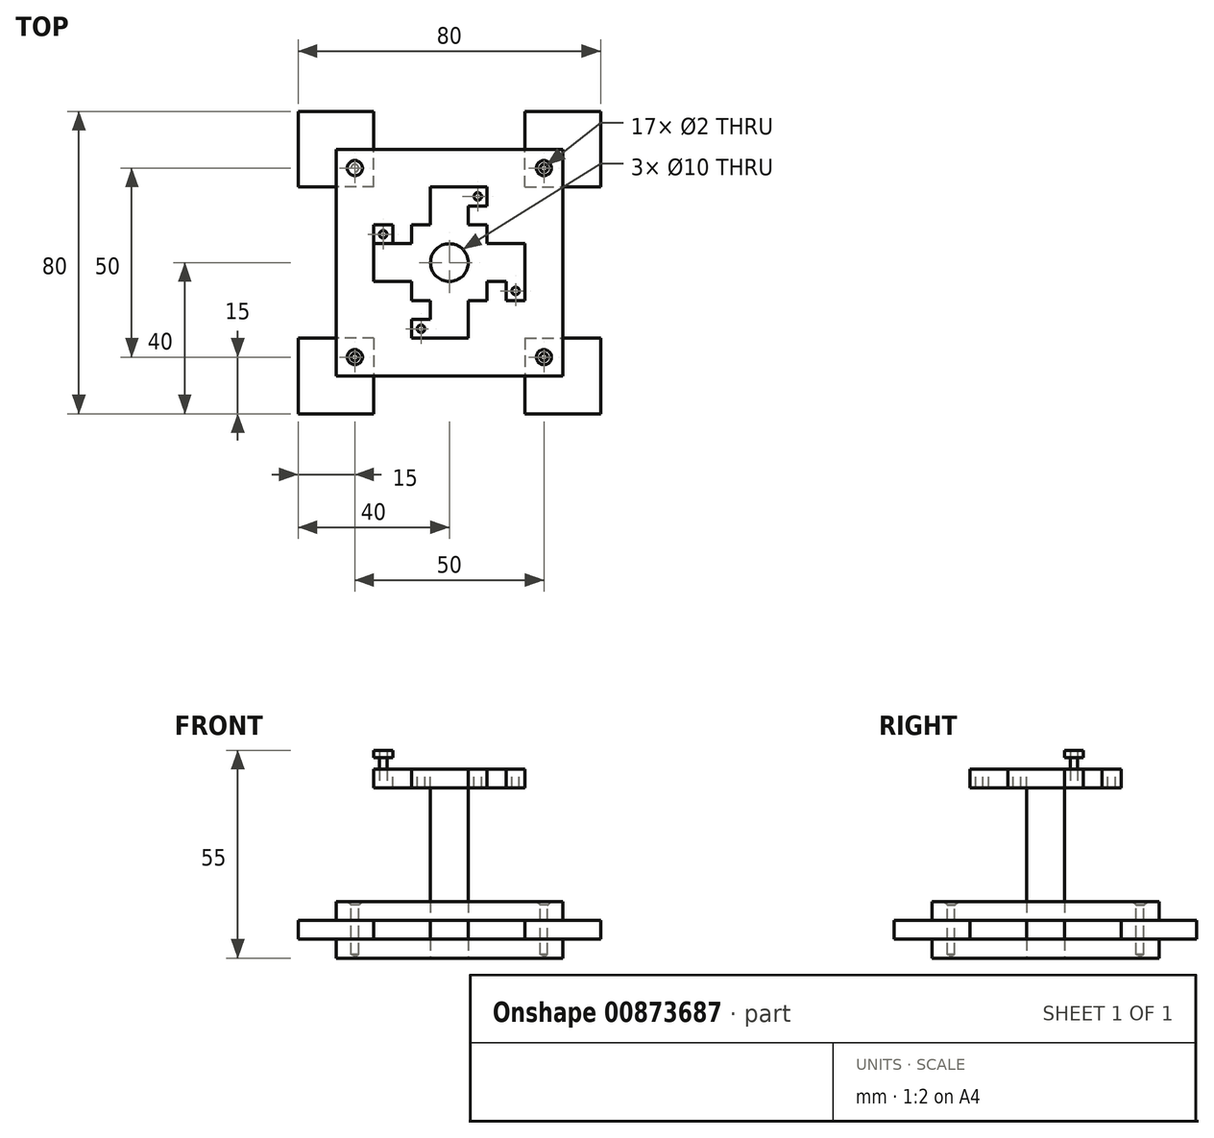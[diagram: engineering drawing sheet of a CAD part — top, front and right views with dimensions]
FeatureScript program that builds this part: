
annotation { "Feature Type Name" : "Feature", "Feature Type Description" : "" }
export const myFeature = defineFeature(function(context is Context, id is Id, definition is map)
    precondition{}
    {
        {
            var Q0;
            Q0=qCreatedBy(makeId("Top.planeOp"),FACE);
            var sketch = newSketch(context, id + "F0", { "sketchPlane" : qUnion([Q0])});
            skLineSegment(sketch, "E0.bottom", {"start": v(-30, 30) * mm, "end": v(30, 30) * mm});
            skLineSegment(sketch, "E0.top", {"start": v(-30, -30) * mm, "end": v(30, -30) * mm});
            skLineSegment(sketch, "E0.left", {"start": v(-30, 30) * mm, "end": v(-30, -30) * mm});
            skLineSegment(sketch, "E0.right", {"start": v(30, 30) * mm, "end": v(30, -30) * mm});
            skPoint(sketch, "E0.middle", {"position": v(0, 0) * mm});
            skSolve(sketch);
        }
        {
            var Q0;
            Q0 = qSketchRegion(id + "F0", true);
            extrude(context, id + "F1", {"entities" : qUnion([Q0]), "depth" : 5 * mm, "offsetDistance" : 25 * mm});
        }
        {
            var Q0;
            Q0=makeQuery(id+"F1.opExtrude","CAP_FACE",FACE,{"disambiguationData":[OSD([sQuery(id+"F0.wireOp",EDGE,"E0.bottom"),sQuery(id+"F0.wireOp",EDGE,"E0.top"),sQuery(id+"F0.wireOp",EDGE,"E0.left"),sQuery(id+"F0.wireOp",EDGE,"E0.right")])],"isStart":false});
            var sketch = newSketch(context, id + "F2", { "sketchPlane" : qUnion([Q0])});
            skLineSegment(sketch, "E1.bottom", {"start": v(-20, 20) * mm, "end": v(-40, 20) * mm});
            skLineSegment(sketch, "E1.top", {"start": v(-20, 40) * mm, "end": v(-40, 40) * mm});
            skLineSegment(sketch, "E1.left", {"start": v(-20, 20) * mm, "end": v(-20, 40) * mm});
            skLineSegment(sketch, "E1.right", {"start": v(-40, 20) * mm, "end": v(-40, 40) * mm});
            skPoint(sketch, "E1.middle", {"position": v(-30, 30) * mm});
            skSolve(sketch);
        }
        {
            var Q0;
            Q0 = qSketchRegion(id + "F2", true);
            extrude(context, id + "F3", {"entities" : qUnion([Q0]), "depth" : 5 * mm, "offsetDistance" : 25 * mm});
        }
        {
            var Q0;
            Q0=makeQuery(id+"F3.opExtrude","CAP_FACE",FACE,{"disambiguationData":[OSD([sQuery(id+"F2.wireOp",EDGE,"E1.bottom"),sQuery(id+"F2.wireOp",EDGE,"E1.top"),sQuery(id+"F2.wireOp",EDGE,"E1.left"),sQuery(id+"F2.wireOp",EDGE,"E1.right")])],"isStart":false});
            var sketch = newSketch(context, id + "F4", { "sketchPlane" : qUnion([Q0])});
            skPoint(sketch, "E2.middle", {"position": v(0, 0) * mm});
            skLineSegment(sketch, "E3.0.0", {"start": v(-30, 30) * mm, "end": v(-30, -30) * mm});
            skLineSegment(sketch, "E3.0.1", {"start": v(-30, -30) * mm, "end": v(30, -30) * mm});
            skLineSegment(sketch, "E3.0.2", {"start": v(30, -30) * mm, "end": v(30, 30) * mm});
            skLineSegment(sketch, "E3.0.3", {"start": v(30, 30) * mm, "end": v(-30, 30) * mm});
            skSolve(sketch);
        }
        {
            var Q0;
            Q0 = qSketchRegion(id + "F4", true);
            extrude(context, id + "F5", {"entities" : qUnion([Q0]), "depth" : 5 * mm, "offsetDistance" : 25 * mm});
        }
        {
            var Q0;
            Q0=makeQuery(id+"F3.opExtrude","SWEPT_BODY",BODY,{"disambiguationData":[OSD([sQuery(id+"F2.wireOp",EDGE,"E1.bottom"),sQuery(id+"F2.wireOp",EDGE,"E1.top"),sQuery(id+"F2.wireOp",EDGE,"E1.left"),sQuery(id+"F2.wireOp",EDGE,"E1.right")])]});
            var Q1;
            Q1=qCreatedBy(makeId("Right.planeOp"),FACE);
            mirror(context, id + "F6", {"entities" : qUnion([Q0]), "mirrorPlane" : qUnion([Q1])});
        }
        {
            var Q0;
            Q0=makeQuery(id+"F3.opExtrude","SWEPT_BODY",BODY,{"disambiguationData":[OSD([sQuery(id+"F2.wireOp",EDGE,"E1.bottom"),sQuery(id+"F2.wireOp",EDGE,"E1.top"),sQuery(id+"F2.wireOp",EDGE,"E1.left"),sQuery(id+"F2.wireOp",EDGE,"E1.right")])]});
            var Q1;
            Q1=makeQuery(id+"F6.opPattern","COPY",BODY,{"derivedFrom":makeQuery(id+"F3.opExtrude","SWEPT_BODY",BODY,{"disambiguationData":[OSD([sQuery(id+"F2.wireOp",EDGE,"E1.bottom"),sQuery(id+"F2.wireOp",EDGE,"E1.top"),sQuery(id+"F2.wireOp",EDGE,"E1.left"),sQuery(id+"F2.wireOp",EDGE,"E1.right")])]}),"instanceName":"1"});
            var Q2;
            Q2=qCreatedBy(makeId("Front.planeOp"),FACE);
            mirror(context, id + "F7", {"entities" : qUnion([Q0, Q1]), "mirrorPlane" : qUnion([Q2])});
        }
        {
            var Q0;
            Q0=makeQuery(id+"F5.opExtrude","CAP_FACE",FACE,{"disambiguationData":[OSD([sQuery(id+"F4.wireOp",EDGE,"E3.0.0"),sQuery(id+"F4.wireOp",EDGE,"E3.0.1"),sQuery(id+"F4.wireOp",EDGE,"E3.0.2"),sQuery(id+"F4.wireOp",EDGE,"E3.0.3")])],"isStart":false});
            var sketch = newSketch(context, id + "F8", { "sketchPlane" : qUnion([Q0])});
            skPoint(sketch, "E4", {"position": v(-25, 25) * mm});
            skPoint(sketch, "E5.MirrorP", {"position": v(-25, -25) * mm});
            skPoint(sketch, "E6.MirrorP", {"position": v(25, 25) * mm});
            skPoint(sketch, "E7.MirrorP", {"position": v(25, -25) * mm});
            skSolve(sketch);
        }
        {
            var Q0;
            Q0=sQuery(id+"F8.wireOp",VERTEX,"E4");
            var Q1;
            Q1=sQuery(id+"F8.wireOp",VERTEX,"E6.MirrorP");
            var Q2;
            Q2=sQuery(id+"F8.wireOp",VERTEX,"E5.MirrorP");
            var Q3;
            Q3=sQuery(id+"F8.wireOp",VERTEX,"E7.MirrorP");
            var Q4;
            Q4=makeQuery(id+"F3.opExtrude","SWEPT_BODY",BODY,{"disambiguationData":[OSD([sQuery(id+"F2.wireOp",EDGE,"E1.bottom"),sQuery(id+"F2.wireOp",EDGE,"E1.top"),sQuery(id+"F2.wireOp",EDGE,"E1.left"),sQuery(id+"F2.wireOp",EDGE,"E1.right")])]});
            var Q5;
            Q5=makeQuery(id+"F6.opPattern","COPY",BODY,{"derivedFrom":makeQuery(id+"F3.opExtrude","SWEPT_BODY",BODY,{"disambiguationData":[OSD([sQuery(id+"F2.wireOp",EDGE,"E1.bottom"),sQuery(id+"F2.wireOp",EDGE,"E1.top"),sQuery(id+"F2.wireOp",EDGE,"E1.left"),sQuery(id+"F2.wireOp",EDGE,"E1.right")])]}),"instanceName":"1"});
            var Q6;
            Q6=makeQuery(id+"F1.opExtrude","SWEPT_BODY",BODY,{"disambiguationData":[OSD([sQuery(id+"F0.wireOp",EDGE,"E0.bottom"),sQuery(id+"F0.wireOp",EDGE,"E0.top"),sQuery(id+"F0.wireOp",EDGE,"E0.left"),sQuery(id+"F0.wireOp",EDGE,"E0.right")])]});
            var Q7;
            Q7=makeQuery(id+"F5.opExtrude","SWEPT_BODY",BODY,{"disambiguationData":[OSD([sQuery(id+"F4.wireOp",EDGE,"E3.0.0"),sQuery(id+"F4.wireOp",EDGE,"E3.0.1"),sQuery(id+"F4.wireOp",EDGE,"E3.0.2"),sQuery(id+"F4.wireOp",EDGE,"E3.0.3")])]});
            var Q8;
            Q8=makeQuery(id+"F7.opPattern","COPY",BODY,{"derivedFrom":makeQuery(id+"F3.opExtrude","SWEPT_BODY",BODY,{"disambiguationData":[OSD([sQuery(id+"F2.wireOp",EDGE,"E1.bottom"),sQuery(id+"F2.wireOp",EDGE,"E1.top"),sQuery(id+"F2.wireOp",EDGE,"E1.left"),sQuery(id+"F2.wireOp",EDGE,"E1.right")])]}),"instanceName":"1"});
            var Q9;
            Q9=makeQuery(id+"F7.opPattern","COPY",BODY,{"derivedFrom":makeQuery(id+"F6.opPattern","COPY",BODY,{"derivedFrom":makeQuery(id+"F3.opExtrude","SWEPT_BODY",BODY,{"disambiguationData":[OSD([sQuery(id+"F2.wireOp",EDGE,"E1.bottom"),sQuery(id+"F2.wireOp",EDGE,"E1.top"),sQuery(id+"F2.wireOp",EDGE,"E1.left"),sQuery(id+"F2.wireOp",EDGE,"E1.right")])]}),"instanceName":"1"}),"instanceName":"1"});
            hole(context, id + "F9", {"style" : HoleStyle.C_SINK, "endStyle" : HoleEndStyle.BLIND, "holeDiameter" : 2 * mm, "cSinkDiameter" : 4 * mm, "cSinkAngle" : 90 * degree, "majorDiameter" : 5 * mm, "holeDepth" : 14 * mm, "isTappedThrough" : true, "tappedDepth" : 12 * mm, "tapClearance" : 3, "startFromSketch" : true, "locations" : qUnion([Q0, Q1, Q2, Q3]), "scope" : qUnion([Q4, Q5, Q6, Q7, Q8, Q9])});
        }
        {
            var Q0;
            Q0=makeQuery(id+"F5.opExtrude","CAP_FACE",FACE,{"disambiguationData":[OSD([sQuery(id+"F4.wireOp",EDGE,"E3.0.0"),sQuery(id+"F4.wireOp",EDGE,"E3.0.1"),sQuery(id+"F4.wireOp",EDGE,"E3.0.2"),sQuery(id+"F4.wireOp",EDGE,"E3.0.3")])],"isStart":false});
            var sketch = newSketch(context, id + "F10", { "sketchPlane" : qUnion([Q0])});
            skCircle(sketch, "E8.0", {"center": v(-25, 25) * mm, "radius": 2 * mm});
            skSolve(sketch);
        }
        {
            var Q0;
            Q0 = qSketchRegion(id + "F10", true);
            var Q1;
            Q1=makeQuery(id+"F1.opExtrude","CAP_FACE",FACE,{"disambiguationData":[OSD([sQuery(id+"F0.wireOp",EDGE,"E0.bottom"),sQuery(id+"F0.wireOp",EDGE,"E0.top"),sQuery(id+"F0.wireOp",EDGE,"E0.left"),sQuery(id+"F0.wireOp",EDGE,"E0.right")])],"isStart":true});
            extrude(context, id + "F11", {"entities" : qUnion([Q0]), "endBound" : BoundingType.UP_TO_SURFACE, "oppositeDirection" : true, "depth" : 25 * mm, "endBoundEntityFace" : qUnion([Q1]), "offsetDistance" : 25 * mm});
        }
        {
            var Q0;
            Q0=makeQuery(id+"F5.opExtrude","SWEPT_BODY",BODY,{"disambiguationData":[OSD([sQuery(id+"F4.wireOp",EDGE,"E3.0.0"),sQuery(id+"F4.wireOp",EDGE,"E3.0.1"),sQuery(id+"F4.wireOp",EDGE,"E3.0.2"),sQuery(id+"F4.wireOp",EDGE,"E3.0.3")])]});
            var Q1;
            Q1=makeQuery(id+"F3.opExtrude","SWEPT_BODY",BODY,{"disambiguationData":[OSD([sQuery(id+"F2.wireOp",EDGE,"E1.bottom"),sQuery(id+"F2.wireOp",EDGE,"E1.top"),sQuery(id+"F2.wireOp",EDGE,"E1.left"),sQuery(id+"F2.wireOp",EDGE,"E1.right")])]});
            var Q2;
            Q2=makeQuery(id+"F1.opExtrude","SWEPT_BODY",BODY,{"disambiguationData":[OSD([sQuery(id+"F0.wireOp",EDGE,"E0.bottom"),sQuery(id+"F0.wireOp",EDGE,"E0.top"),sQuery(id+"F0.wireOp",EDGE,"E0.left"),sQuery(id+"F0.wireOp",EDGE,"E0.right")])]});
            var Q3;
            Q3=makeQuery(id+"F11.opExtrude","SWEPT_BODY",BODY,{"disambiguationData":[OSD([sQuery(id+"F10.wireOp",EDGE,"E8.0")])]});
            booleanBodies(context, id + "F12", {"operationType" : BooleanOperationType.SUBTRACTION, "tools" : qUnion([Q0, Q1, Q2]), "targets" : qUnion([Q3]), "keepTools" : true});
        }
        {
            var Q0;
            Q0=qCreatedBy(makeId("Top.planeOp"),FACE);
            var sketch = newSketch(context, id + "F13", { "sketchPlane" : qUnion([Q0])});
            skCircle(sketch, "E9", {"center": v(0, 0) * mm, "radius": 5 * mm});
            skSolve(sketch);
        }
        {
            var Q0;
            Q0 = qSketchRegion(id + "F13", true);
            extrude(context, id + "F14", {"entities" : qUnion([Q0]), "depth" : 50 * mm, "offsetDistance" : 25 * mm});
        }
        {
            var Q0;
            Q0=makeQuery(id+"F14.opExtrude","CAP_FACE",FACE,{"disambiguationData":[OSD([sQuery(id+"F13.wireOp",EDGE,"E9")])],"isStart":false});
            var sketch = newSketch(context, id + "F15", { "sketchPlane" : qUnion([Q0])});
            skLineSegment(sketch, "E10", {"start": v(-5, 10) * mm, "end": v(-10, 10) * mm});
            skLineSegment(sketch, "E11", {"start": v(-10, 10) * mm, "end": v(-10, 5) * mm});
            skLineSegment(sketch, "E12", {"start": v(-5, 10) * mm, "end": v(-5, 20) * mm});
            skLineSegment(sketch, "E13", {"start": v(-5, 20) * mm, "end": v(10, 20) * mm});
            skLineSegment(sketch, "E14", {"start": v(10, 20) * mm, "end": v(10, 15) * mm});
            skLineSegment(sketch, "E15", {"start": v(10, 15) * mm, "end": v(5, 15) * mm});
            skLineSegment(sketch, "E16", {"start": v(5, 15) * mm, "end": v(5, 10) * mm});
            skLineSegment(sketch, "E17", {"start": v(5, 10) * mm, "end": v(10, 10) * mm});
            skLineSegment(sketch, "E18", {"start": v(10, 10) * mm, "end": v(10, 5) * mm});
            skLineSegment(sketch, "E19", {"start": v(10, 5) * mm, "end": v(20, 5) * mm});
            skLineSegment(sketch, "E20", {"start": v(20, 5) * mm, "end": v(20, -10) * mm});
            skLineSegment(sketch, "E21", {"start": v(20, -10) * mm, "end": v(15, -10) * mm});
            skLineSegment(sketch, "E22", {"start": v(15, -10) * mm, "end": v(15, -5) * mm});
            skLineSegment(sketch, "E23", {"start": v(15, -5) * mm, "end": v(10, -5) * mm});
            skLineSegment(sketch, "E24", {"start": v(10, -5) * mm, "end": v(10, -10) * mm});
            skLineSegment(sketch, "E25", {"start": v(10, -10) * mm, "end": v(5, -10) * mm});
            skLineSegment(sketch, "E26", {"start": v(5, -10) * mm, "end": v(5, -20) * mm});
            skLineSegment(sketch, "E27", {"start": v(5, -20) * mm, "end": v(-10, -20) * mm});
            skLineSegment(sketch, "E28", {"start": v(-10, -20) * mm, "end": v(-10, -15) * mm});
            skLineSegment(sketch, "E29", {"start": v(-10, -15) * mm, "end": v(-5, -15) * mm});
            skLineSegment(sketch, "E30", {"start": v(-5, -15) * mm, "end": v(-5, -10) * mm});
            skLineSegment(sketch, "E31", {"start": v(-5, -10) * mm, "end": v(-10, -10) * mm});
            skLineSegment(sketch, "E32", {"start": v(-10, -10) * mm, "end": v(-10, -5) * mm});
            skLineSegment(sketch, "E33", {"start": v(-10, -5) * mm, "end": v(-20, -5) * mm});
            skLineSegment(sketch, "E34", {"start": v(-20, -5) * mm, "end": v(-20, 10) * mm});
            skLineSegment(sketch, "E35", {"start": v(-20, 10) * mm, "end": v(-15, 10) * mm});
            skLineSegment(sketch, "E36", {"start": v(-15, 10) * mm, "end": v(-15, 5) * mm});
            skLineSegment(sketch, "E37", {"start": v(-15, 5) * mm, "end": v(-10, 5) * mm});
            skPoint(sketch, "E38", {"position": v(-5, 15) * mm});
            skPoint(sketch, "E39", {"position": v(-15, -5) * mm});
            skPoint(sketch, "E40", {"position": v(15, 5) * mm});
            skPoint(sketch, "E41", {"position": v(5, -15) * mm});
            skPoint(sketch, "E42", {"position": v(0, 0) * mm});
            skSolve(sketch);
        }
        {
            var Q0;
            Q0 = qSketchRegion(id + "F15", true);
            extrude(context, id + "F16", {"entities" : qUnion([Q0]), "oppositeDirection" : true, "depth" : 5 * mm, "offsetDistance" : 25 * mm});
        }
        {
            var Q0;
            Q0=makeQuery(id+"F14.opExtrude","SWEPT_BODY",BODY,{"disambiguationData":[OSD([sQuery(id+"F13.wireOp",EDGE,"E9")])]});
            var Q1;
            Q1=makeQuery(id+"F16.opExtrude","SWEPT_BODY",BODY,{"disambiguationData":[OSD([sQuery(id+"F15.wireOp",EDGE,"E10"),sQuery(id+"F15.wireOp",EDGE,"E11"),sQuery(id+"F15.wireOp",EDGE,"E12"),sQuery(id+"F15.wireOp",EDGE,"E13"),sQuery(id+"F15.wireOp",EDGE,"E14"),sQuery(id+"F15.wireOp",EDGE,"E15"),sQuery(id+"F15.wireOp",EDGE,"E16"),sQuery(id+"F15.wireOp",EDGE,"E17"),sQuery(id+"F15.wireOp",EDGE,"E18"),sQuery(id+"F15.wireOp",EDGE,"E19"),sQuery(id+"F15.wireOp",EDGE,"E20"),sQuery(id+"F15.wireOp",EDGE,"E21"),sQuery(id+"F15.wireOp",EDGE,"E22"),sQuery(id+"F15.wireOp",EDGE,"E23"),sQuery(id+"F15.wireOp",EDGE,"E24"),sQuery(id+"F15.wireOp",EDGE,"E25"),sQuery(id+"F15.wireOp",EDGE,"E26"),sQuery(id+"F15.wireOp",EDGE,"E27"),sQuery(id+"F15.wireOp",EDGE,"E28"),sQuery(id+"F15.wireOp",EDGE,"E29"),sQuery(id+"F15.wireOp",EDGE,"E30"),sQuery(id+"F15.wireOp",EDGE,"E31"),sQuery(id+"F15.wireOp",EDGE,"E32"),sQuery(id+"F15.wireOp",EDGE,"E33"),sQuery(id+"F15.wireOp",EDGE,"E34"),sQuery(id+"F15.wireOp",EDGE,"E35"),sQuery(id+"F15.wireOp",EDGE,"E36"),sQuery(id+"F15.wireOp",EDGE,"E37")])]});
            var Q2;
            Q2=makeQuery(id+"F5.opExtrude","SWEPT_BODY",BODY,{"disambiguationData":[OSD([sQuery(id+"F4.wireOp",EDGE,"E3.0.0"),sQuery(id+"F4.wireOp",EDGE,"E3.0.1"),sQuery(id+"F4.wireOp",EDGE,"E3.0.2"),sQuery(id+"F4.wireOp",EDGE,"E3.0.3")])]});
            var Q3;
            Q3=makeQuery(id+"F1.opExtrude","SWEPT_BODY",BODY,{"disambiguationData":[OSD([sQuery(id+"F0.wireOp",EDGE,"E0.bottom"),sQuery(id+"F0.wireOp",EDGE,"E0.top"),sQuery(id+"F0.wireOp",EDGE,"E0.left"),sQuery(id+"F0.wireOp",EDGE,"E0.right")])]});
            booleanBodies(context, id + "F17", {"operationType" : BooleanOperationType.SUBTRACTION, "tools" : qUnion([Q0]), "targets" : qUnion([Q1, Q2, Q3]), "keepTools" : true});
        }
        {
            var Q0;
            Q0=makeQuery(id+"F16.opExtrude","CAP_FACE",FACE,{"disambiguationData":[OSD([sQuery(id+"F15.wireOp",EDGE,"E10"),sQuery(id+"F15.wireOp",EDGE,"E11"),sQuery(id+"F15.wireOp",EDGE,"E12"),sQuery(id+"F15.wireOp",EDGE,"E13"),sQuery(id+"F15.wireOp",EDGE,"E14"),sQuery(id+"F15.wireOp",EDGE,"E15"),sQuery(id+"F15.wireOp",EDGE,"E16"),sQuery(id+"F15.wireOp",EDGE,"E17"),sQuery(id+"F15.wireOp",EDGE,"E18"),sQuery(id+"F15.wireOp",EDGE,"E19"),sQuery(id+"F15.wireOp",EDGE,"E20"),sQuery(id+"F15.wireOp",EDGE,"E21"),sQuery(id+"F15.wireOp",EDGE,"E22"),sQuery(id+"F15.wireOp",EDGE,"E23"),sQuery(id+"F15.wireOp",EDGE,"E24"),sQuery(id+"F15.wireOp",EDGE,"E25"),sQuery(id+"F15.wireOp",EDGE,"E26"),sQuery(id+"F15.wireOp",EDGE,"E27"),sQuery(id+"F15.wireOp",EDGE,"E28"),sQuery(id+"F15.wireOp",EDGE,"E29"),sQuery(id+"F15.wireOp",EDGE,"E30"),sQuery(id+"F15.wireOp",EDGE,"E31"),sQuery(id+"F15.wireOp",EDGE,"E32"),sQuery(id+"F15.wireOp",EDGE,"E33"),sQuery(id+"F15.wireOp",EDGE,"E34"),sQuery(id+"F15.wireOp",EDGE,"E35"),sQuery(id+"F15.wireOp",EDGE,"E36"),sQuery(id+"F15.wireOp",EDGE,"E37")])],"isStart":true});
            var sketch = newSketch(context, id + "F18", { "sketchPlane" : qUnion([Q0])});
            skCircle(sketch, "E43", {"center": v(-17.5, 7.5) * mm, "radius": 1 * mm});
            skSolve(sketch);
        }
        {
            var Q0;
            Q0 = qSketchRegion(id + "F18", true);
            extrude(context, id + "F19", {"entities" : qUnion([Q0]), "endBound" : BoundingType.SYMMETRIC, "depth" : 10 * mm, "offsetDistance" : 25 * mm});
        }
        {
            var Q0;
            Q0=makeQuery(id+"F19.opExtrude","CAP_FACE",FACE,{"disambiguationData":[OSD([sQuery(id+"F18.wireOp",EDGE,"E43")])],"isStart":false});
            var sketch = newSketch(context, id + "F20", { "sketchPlane" : qUnion([Q0])});
            skLineSegment(sketch, "E44.bottom", {"start": v(-20, 10) * mm, "end": v(-15, 10) * mm});
            skLineSegment(sketch, "E44.top", {"start": v(-20, 5) * mm, "end": v(-15, 5) * mm});
            skLineSegment(sketch, "E44.left", {"start": v(-20, 10) * mm, "end": v(-20, 5) * mm});
            skLineSegment(sketch, "E44.right", {"start": v(-15, 10) * mm, "end": v(-15, 5) * mm});
            skPoint(sketch, "E44.middle", {"position": v(-17.5, 7.5) * mm});
            skSolve(sketch);
        }
        {
            var Q0;
            Q0 = qSketchRegion(id + "F20", true);
            extrude(context, id + "F21", {"entities" : qUnion([Q0]), "oppositeDirection" : true, "depth" : 2 * mm, "offsetDistance" : 25 * mm});
        }
        {
            var Q0;
            Q0=makeQuery(id+"F19.opExtrude","SWEPT_BODY",BODY,{"disambiguationData":[OSD([sQuery(id+"F18.wireOp",EDGE,"E43")])]});
            var Q1;
            Q1=makeQuery(id+"F16.opExtrude","SWEPT_BODY",BODY,{"disambiguationData":[OSD([sQuery(id+"F15.wireOp",EDGE,"E10"),sQuery(id+"F15.wireOp",EDGE,"E11"),sQuery(id+"F15.wireOp",EDGE,"E12"),sQuery(id+"F15.wireOp",EDGE,"E13"),sQuery(id+"F15.wireOp",EDGE,"E14"),sQuery(id+"F15.wireOp",EDGE,"E15"),sQuery(id+"F15.wireOp",EDGE,"E16"),sQuery(id+"F15.wireOp",EDGE,"E17"),sQuery(id+"F15.wireOp",EDGE,"E18"),sQuery(id+"F15.wireOp",EDGE,"E19"),sQuery(id+"F15.wireOp",EDGE,"E20"),sQuery(id+"F15.wireOp",EDGE,"E21"),sQuery(id+"F15.wireOp",EDGE,"E22"),sQuery(id+"F15.wireOp",EDGE,"E23"),sQuery(id+"F15.wireOp",EDGE,"E24"),sQuery(id+"F15.wireOp",EDGE,"E25"),sQuery(id+"F15.wireOp",EDGE,"E26"),sQuery(id+"F15.wireOp",EDGE,"E27"),sQuery(id+"F15.wireOp",EDGE,"E28"),sQuery(id+"F15.wireOp",EDGE,"E29"),sQuery(id+"F15.wireOp",EDGE,"E30"),sQuery(id+"F15.wireOp",EDGE,"E31"),sQuery(id+"F15.wireOp",EDGE,"E32"),sQuery(id+"F15.wireOp",EDGE,"E33"),sQuery(id+"F15.wireOp",EDGE,"E34"),sQuery(id+"F15.wireOp",EDGE,"E35"),sQuery(id+"F15.wireOp",EDGE,"E36"),sQuery(id+"F15.wireOp",EDGE,"E37")])]});
            var Q2;
            Q2=makeQuery(id+"F21.opExtrude","SWEPT_BODY",BODY,{"disambiguationData":[OSD([sQuery(id+"F20.wireOp",EDGE,"E44.bottom"),sQuery(id+"F20.wireOp",EDGE,"E44.top"),sQuery(id+"F20.wireOp",EDGE,"E44.left"),sQuery(id+"F20.wireOp",EDGE,"E44.right")])]});
            booleanBodies(context, id + "F22", {"operationType" : BooleanOperationType.SUBTRACTION, "tools" : qUnion([Q0]), "targets" : qUnion([Q1, Q2]), "keepTools" : true});
        }
        {
            var Q0;
            Q0=makeQuery(id+"F16.opExtrude","CAP_FACE",FACE,{"disambiguationData":[OSD([sQuery(id+"F15.wireOp",EDGE,"E10"),sQuery(id+"F15.wireOp",EDGE,"E11"),sQuery(id+"F15.wireOp",EDGE,"E12"),sQuery(id+"F15.wireOp",EDGE,"E13"),sQuery(id+"F15.wireOp",EDGE,"E14"),sQuery(id+"F15.wireOp",EDGE,"E15"),sQuery(id+"F15.wireOp",EDGE,"E16"),sQuery(id+"F15.wireOp",EDGE,"E17"),sQuery(id+"F15.wireOp",EDGE,"E18"),sQuery(id+"F15.wireOp",EDGE,"E19"),sQuery(id+"F15.wireOp",EDGE,"E20"),sQuery(id+"F15.wireOp",EDGE,"E21"),sQuery(id+"F15.wireOp",EDGE,"E22"),sQuery(id+"F15.wireOp",EDGE,"E23"),sQuery(id+"F15.wireOp",EDGE,"E24"),sQuery(id+"F15.wireOp",EDGE,"E25"),sQuery(id+"F15.wireOp",EDGE,"E26"),sQuery(id+"F15.wireOp",EDGE,"E27"),sQuery(id+"F15.wireOp",EDGE,"E28"),sQuery(id+"F15.wireOp",EDGE,"E29"),sQuery(id+"F15.wireOp",EDGE,"E30"),sQuery(id+"F15.wireOp",EDGE,"E31"),sQuery(id+"F15.wireOp",EDGE,"E32"),sQuery(id+"F15.wireOp",EDGE,"E33"),sQuery(id+"F15.wireOp",EDGE,"E34"),sQuery(id+"F15.wireOp",EDGE,"E35"),sQuery(id+"F15.wireOp",EDGE,"E36"),sQuery(id+"F15.wireOp",EDGE,"E37")])],"isStart":true});
            var sketch = newSketch(context, id + "F23", { "sketchPlane" : qUnion([Q0])});
            skCircle(sketch, "E45", {"center": v(-7.5, -17.5) * mm, "radius": 1 * mm});
            skCircle(sketch, "E46", {"center": v(17.5, -7.5) * mm, "radius": 1 * mm});
            skPoint(sketch, "E46.centerSnap0", {"position": v(17.5, -10) * mm});
            skCircle(sketch, "E47", {"center": v(7.5, 17.5) * mm, "radius": 1 * mm});
            skSolve(sketch);
        }
        {
            var Q0;
            Q0 = qSketchRegion(id + "F23", true);
            extrude(context, id + "F24", {"entities" : qUnion([Q0]), "operationType" : NewBodyOperationType.REMOVE, "oppositeDirection" : true, "depth" : 10 * mm, "offsetDistance" : 25 * mm});
        }
    });
